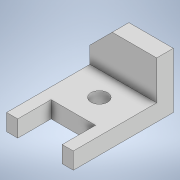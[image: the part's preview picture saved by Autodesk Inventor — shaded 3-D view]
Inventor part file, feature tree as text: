
AUTODESK INVENTOR PART (.ipt)
format: ipt  version: 2022.2 (Build 262287030, 287C)  size: 125,440 bytes
history: native  units: in
note: dims shown in document units (in); Inventor stores cm internally (conversion verified against a paired STEP export)
features: extrude x3, sketch x3
ambient origin geometry x8: Origin, YZ Plane, XZ Plane, XY Plane, X Axis, Y Axis, Z Axis, Center Point
bodies: Solid1 (feature_tree)
feature tree (6):
  extrude  "Extrusion1"  Depth=2.5in
  extrude  "Extrusion2"  Depth=3.0in TaperAngle=0.0deg
  extrude  "Extrusion3"  Depth=2.0in
  sketch  "Sketch2"  dims[d0=4.5in d1=2.5in]
  sketch  "Sketch3"  dims[d2=0.75in d3=3.0in d4=0.0in]
  sketch  "Sketch4"  dims[d5=0.5in d6=2.0in d7=1.5in d8=1.5in d9=2.67in d10=0.75in d11=0.0in d12=0.0in d13=2.0in d14=1.0in d15=0.0in d16=0.0in]
